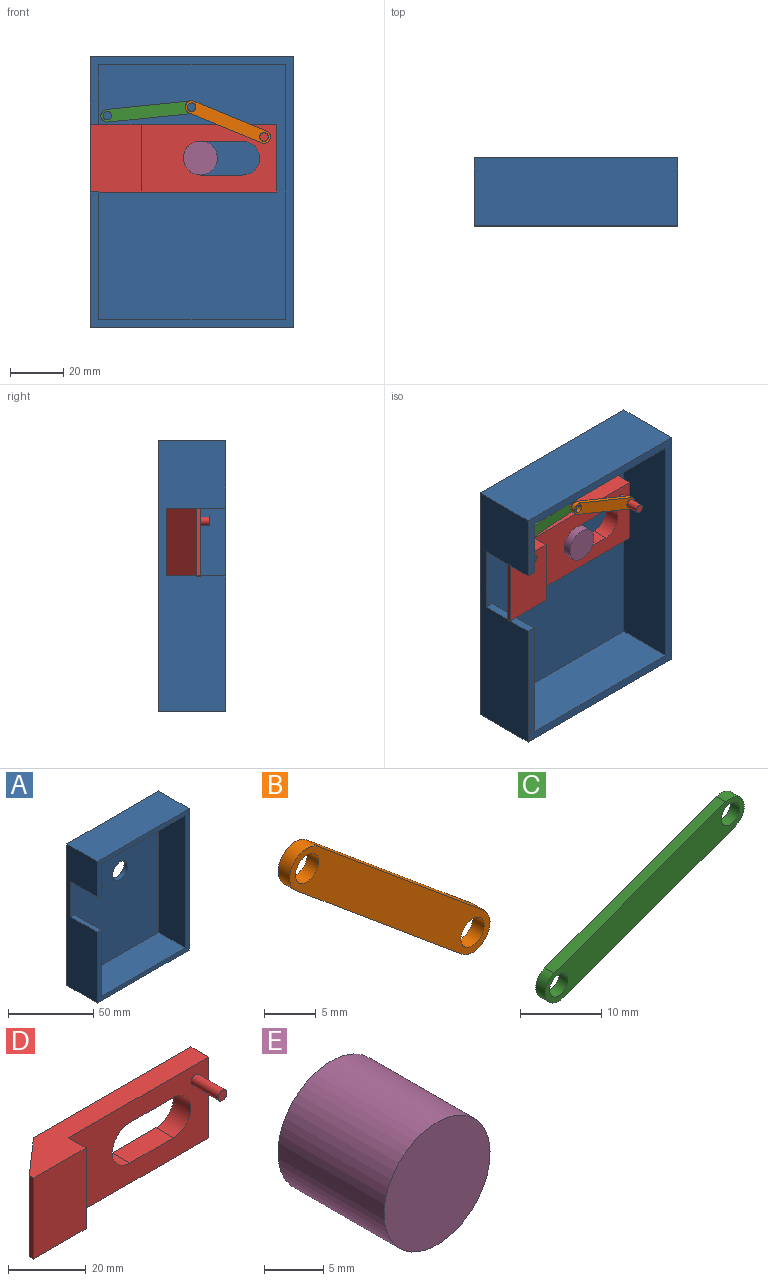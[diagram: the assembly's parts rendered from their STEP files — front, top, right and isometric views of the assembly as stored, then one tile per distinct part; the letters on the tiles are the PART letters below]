
ASSEMBLY  parts=5 mates=9
PART A: 17 faces, bbox 76.2x25.4x101.6 mm
  f0: plane 101.6x76.2mm, normal (0,-1,0), area 1008.1mm2, adj f1,f2,f3,f4,f5,f7,f8,f9
  f1: plane 47.63x22.23mm, normal (1,0,0), area 1058.5mm2, adj f0,f10,f11,f13
  f2: plane 76.2x25.4mm, normal (0,0,-1), area 1935.5mm2, adj f0,f3,f5,f6
  f3: plane 101.6x25.4mm, normal (1,0,0), area 2580.6mm2, adj f0,f2,f4,f6
  f4: plane 76.2x25.4mm, normal (0,0,1), area 1935.5mm2, adj f0,f3,f5,f6
  f5: plane 101.6x25.4mm, normal (-1,0,0), area 2016.1mm2, adj f0,f2,f4,f6,f11,f12,f13
  f6: plane 101.6x76.2mm, normal (0,1,0), area 7615.2mm2, adj f2,f3,f4,f5,f14
  f7: plane 95.25x22.23mm, normal (-1,0,0), area 2116.9mm2, adj f0,f8,f10,f11
  f8: plane 69.85x22.23mm, normal (0,0,-1), area 1552.4mm2, adj f0,f7,f9,f11
  f9: plane 22.23x22.23mm, normal (1,0,0), area 494mm2, adj f0,f8,f11,f12
  f10: plane 69.85x22.23mm, normal (0,0,1), area 1552.4mm2, adj f0,f1,f7,f11
  f11: plane 95.25x73.03mm, normal (0,-1,0), area 6599.3mm2, adj f1,f5,f7,f8,f9,f10,f12,f13
  f12: plane 22.23x3.18mm, normal (0,0,-1), area 70.6mm2, adj f0,f5,f9,f11
  f13: plane 22.23x3.18mm, normal (0,0,1), area 70.6mm2, adj f0,f1,f5,f11
  f14: cylinder r=6.35mm len=12.7mm, axis (0,-1,0), area 126.7mm2, adj f6,f11
  f15: cylinder r=1.59mm len=19.05mm, axis (0,1,0), area 190mm2, adj f11,f16
  f16: plane 3.18x3.18mm, normal (0,-1,0), area 7.9mm2, adj f15
PART B: 8 faces, bbox 27.3x1.6x23.6 mm
  f0: plane 22.55x18.79mm, normal (-0.64,0,-0.77), area 46.6mm2, adj f1,f4,f6,f7
  f1: cylinder r=2.38mm len=4.21mm, axis (0,1,0), area 11.9mm2, adj f0,f2,f6,f7
  f2: plane 22.55x18.79mm, normal (0.64,0,0.77), area 46.6mm2, adj f1,f4,f6,f7
  f3: cylinder r=1.59mm len=3.18mm, axis (0,1,0), area 15.8mm2, adj f6,f7
  f4: cylinder r=2.38mm len=4.21mm, axis (0,1,0), area 11.9mm2, adj f0,f2,f6,f7
  f5: cylinder r=1.59mm len=3.18mm, axis (0,1,0), area 15.8mm2, adj f6,f7
  f6: plane 27.31x23.55mm, normal (0,-1,0), area 141.8mm2, adj f0,f1,f2,f3,f4,f5
  f7: plane 27.31x23.55mm, normal (0,1,0), area 141.8mm2, adj f0,f1,f2,f3,f4,f5
PART C: 8 faces, bbox 34.6x1.6x15.6 mm
  f0: plane 29.84x10.85mm, normal (0.34,0,-0.94), area 50.4mm2, adj f1,f4,f6,f7
  f1: cylinder r=2.38mm len=4.62mm, axis (0,1,0), area 11.9mm2, adj f0,f2,f6,f7
  f2: plane 29.84x10.85mm, normal (-0.34,0,0.94), area 50.4mm2, adj f1,f4,f6,f7
  f3: cylinder r=1.59mm len=3.18mm, axis (0,1,0), area 15.8mm2, adj f6,f7
  f4: cylinder r=2.38mm len=4.62mm, axis (0,1,0), area 11.9mm2, adj f0,f2,f6,f7
  f5: cylinder r=1.59mm len=3.18mm, axis (0,1,0), area 15.8mm2, adj f6,f7
  f6: plane 34.6x15.61mm, normal (0,-1,0), area 153.2mm2, adj f0,f1,f2,f3,f4,f5
  f7: plane 34.6x15.61mm, normal (0,1,0), area 153.2mm2, adj f0,f1,f2,f3,f4,f5
PART D: 15 faces, bbox 69.9x16.2x25.4 mm
  f0: plane 25.4x1.59mm, normal (-1,0,0), area 40.3mm2, adj f1,f2,f8,f14
  f1: plane 69.85x12.7mm, normal (0,0,1), area 494mm2, adj f0,f3,f8,f9,f10,f11,f14
  f2: plane 69.85x12.7mm, normal (0,0,-1), area 494mm2, adj f0,f3,f8,f9,f10,f11,f14
  f3: plane 25.4x6.35mm, normal (1,0,0), area 161.3mm2, adj f1,f2,f9,f11
  f4: plane 15.88x6.35mm, normal (0,0,1), area 100.8mm2, adj f5,f7,f9,f11
  f5: cylinder r=6.35mm len=12.7mm, axis (0,-1,0), area 126.7mm2, adj f4,f6,f9,f11
  f6: plane 15.88x6.35mm, normal (0,0,-1), area 100.8mm2, adj f5,f7,f9,f11
  f7: cylinder r=6.35mm len=12.7mm, axis (0,-1,0), area 126.7mm2, adj f4,f6,f9,f11
  f8: plane 25.4x19.05mm, normal (0,-1,0), area 483.9mm2, adj f0,f1,f2,f10
  f9: plane 57.15x25.4mm, normal (0,1,0), area 1123.3mm2, adj f1,f2,f3,f4,f5,f6,f7,f14
  f10: plane 25.4x6.35mm, normal (1,0,0), area 161.3mm2, adj f1,f2,f8,f11
  f11: plane 50.8x25.4mm, normal (0,-1,0), area 954.1mm2, adj f1,f2,f3,f4,f5,f6,f7,f10
  f12: cylinder r=1.59mm len=9.84mm, axis (0,1,0), area 98.2mm2, adj f11,f13
  f13: plane 3.18x3.18mm, normal (0,-1,0), area 7.9mm2, adj f12
  f14: plane 25.4x12.7mm, normal (-0.66,0.75,0), area 428.6mm2, adj f0,f1,f2,f9
PART E: 3 faces, bbox 12.7x12.7x12.7 mm
  f0: cylinder r=6.35mm len=12.7mm, axis (0,1,0), area 506.7mm2, adj f1,f2
  f1: plane 12.7x12.7mm, normal (0,1,0), area 126.7mm2, adj f0
  f2: plane 12.7x12.7mm, normal (0,-1,0), area 126.7mm2, adj f0
PLACE A t=(0.07,0.06,0.18)mm fixed
PLACE B rot(axis=(0,-1,0),17.5deg) t=(13.57,-1.53,-5.07)mm
PLACE C rot(axis=(0,1,0),14.2deg) t=(-7.89,0.06,-6.73)mm
PLACE D t=(0.07,0.06,0.18)mm
PLACE E rot(axis=(-0.02,0.98,-0.19),0deg) t=(0.07,-3.11,0.18)mm
MATE parallel D.f1 <-> A.f12  axis (0,0,1) through (-4.94,-7.77,25.58)mm
MATE pin_slot E.f0 <-> D.f5  axis (0,1,0) through (3.25,0.06,12.88)mm
MATE planar A.f15 <-> C.f3  axis (0,-1,0) through (-31.68,-22.16,28.75)mm
MATE cylindrical E.f0 <-> A.f14  axis (0,1,0) through (3.25,0.06,12.88)mm
MATE planar E.f0 <-> A.f14  axis (0,1,0) through (3.25,0.06,12.88)mm
MATE cylindrical D.f12 <-> B.f1  axis (0,1,0) through (27.06,-14.38,20.82)mm
MATE planar C.f1 <-> B.f4  axis (0,-1,0) through (-0.09,-11.05,31.97)mm
MATE cylindrical C.f1 <-> B.f4  axis (0,-1,0) through (-0.09,-11.05,31.97)mm
MATE cylindrical A.f15 <-> C.f3  axis (0,1,0) through (-31.68,-22.16,28.75)mm
